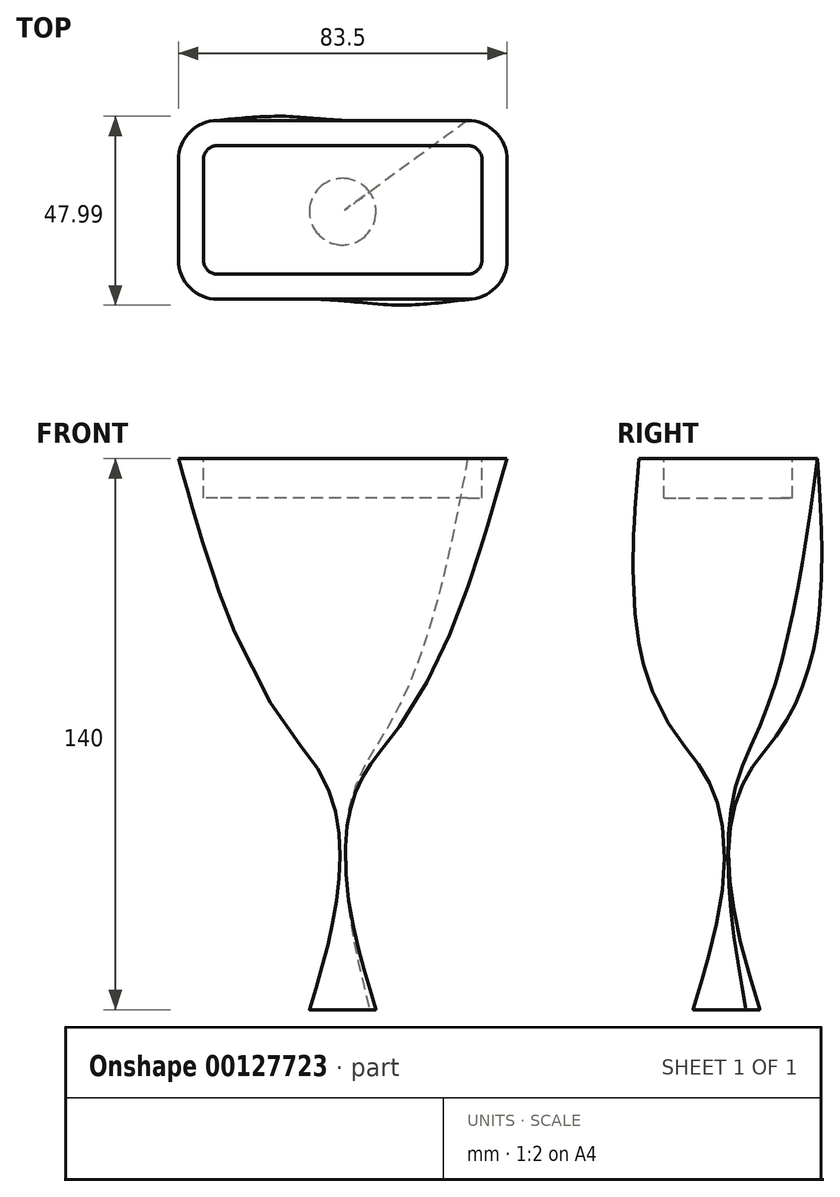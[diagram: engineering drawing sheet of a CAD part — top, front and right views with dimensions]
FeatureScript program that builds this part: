
annotation { "Feature Type Name" : "Feature", "Feature Type Description" : "" }
export const myFeature = defineFeature(function(context is Context, id is Id, definition is map)
    precondition{}
    {
        {
            var Q0;
            Q0=qCreatedBy(makeId("Top.planeOp"),FACE);
            cPlane(context, id + "F0", {"entities" : qUnion([Q0]), "cplaneType" : CPlaneType.OFFSET, "offset" : 60 * mm, "width" : 152.4 * mm, "height" : 152.4 * mm});
        }
        {
            var Q0;
            Q0=qCreatedBy(id+"F0.planeOp",FACE);
            var sketch = newSketch(context, id + "F1", { "sketchPlane" : qUnion([Q0])});
            skLineSegment(sketch, "E0.bottom", {"start": v(31.76, 23.15) * mm, "end": v(-31.74, 23.15) * mm});
            skLineSegment(sketch, "E0.top", {"start": v(31.76, -22.25) * mm, "end": v(-31.74, -22.25) * mm});
            skLineSegment(sketch, "E0.left", {"start": v(41.76, 13.15) * mm, "end": v(41.76, -12.25) * mm});
            skLineSegment(sketch, "E0.right", {"start": v(-41.74, 13.15) * mm, "end": v(-41.74, -12.25) * mm});
            skPoint(sketch, "E0.middle", {"position": v(0.01, 0.45) * mm});
            skPoint(sketch, "E1.visualSharp", {"position": v(-41.74, 23.15) * mm});
            skArc(sketch, "E1.filletArc", {"start": v(-31.74, 23.15) * mm, "mid": v(-38.8, 20.22) * mm, "end": v(-41.74, 13.15) * mm});
            skPoint(sketch, "E2.visualSharp", {"position": v(-41.74, -22.25) * mm});
            skArc(sketch, "E2.filletArc", {"start": v(-41.74, -12.25) * mm, "mid": v(-38.8, -19.32) * mm, "end": v(-31.74, -22.25) * mm});
            skPoint(sketch, "E3.visualSharp", {"position": v(41.76, -22.25) * mm});
            skArc(sketch, "E3.filletArc", {"start": v(31.76, -22.25) * mm, "mid": v(38.84, -19.32) * mm, "end": v(41.76, -12.25) * mm});
            skPoint(sketch, "E4.visualSharp", {"position": v(41.76, 23.15) * mm});
            skArc(sketch, "E4.filletArc", {"start": v(41.76, 13.15) * mm, "mid": v(38.84, 20.22) * mm, "end": v(31.76, 23.15) * mm});
            skSolve(sketch);
        }
        {
            var Q0;
            Q0=qCreatedBy(makeId("Top.planeOp"),FACE);
            cPlane(context, id + "F2", {"entities" : qUnion([Q0]), "cplaneType" : CPlaneType.OFFSET, "offset" : 10 * mm, "oppositeDirection" : true, "width" : 152.4 * mm, "height" : 152.4 * mm});
        }
        {
            var Q0;
            Q0=qCreatedBy(id+"F2.planeOp",FACE);
            var sketch = newSketch(context, id + "F3", { "sketchPlane" : qUnion([Q0])});
            skCircle(sketch, "E5", {"center": v(0, 0) * mm, "radius": 12.93 * mm});
            skSolve(sketch);
        }
        {
            var Q0;
            Q0=qCreatedBy(makeId("Top.planeOp"),FACE);
            cPlane(context, id + "F4", {"entities" : qUnion([Q0]), "cplaneType" : CPlaneType.OFFSET, "offset" : 20 * mm, "oppositeDirection" : true, "width" : 152.4 * mm, "height" : 152.4 * mm});
        }
        {
            var Q0;
            Q0=qCreatedBy(id+"F4.planeOp",FACE);
            var sketch = newSketch(context, id + "F5", { "sketchPlane" : qUnion([Q0])});
            skCircle(sketch, "E6", {"center": v(0, 0) * mm, "radius": 5.59 * mm});
            skSolve(sketch);
        }
        {
            var Q0;
            Q0=qCreatedBy(id+"F4.planeOp",FACE);
            cPlane(context, id + "F6", {"entities" : qUnion([Q0]), "cplaneType" : CPlaneType.OFFSET, "offset" : 50 * mm, "oppositeDirection" : true, "width" : 152.4 * mm, "height" : 152.4 * mm});
        }
        {
            var Q0;
            Q0=qCreatedBy(id+"F6.planeOp",FACE);
            var sketch = newSketch(context, id + "F7", { "sketchPlane" : qUnion([Q0])});
            skCircle(sketch, "E7", {"center": v(0, 0) * mm, "radius": 5.47 * mm});
            skSolve(sketch);
        }
        {
            var Q0;
            Q0=qCreatedBy(id+"F6.planeOp",FACE);
            cPlane(context, id + "F8", {"entities" : qUnion([Q0]), "cplaneType" : CPlaneType.OFFSET, "offset" : 10 * mm, "oppositeDirection" : true, "width" : 152.4 * mm, "height" : 152.4 * mm});
        }
        {
            var Q0;
            Q0=qCreatedBy(id+"F8.planeOp",FACE);
            var sketch = newSketch(context, id + "F9", { "sketchPlane" : qUnion([Q0])});
            skCircle(sketch, "E8", {"center": v(0, 0) * mm, "radius": 8.46 * mm});
            skSolve(sketch);
        }
        {
            var Q0;
            Q0 = qSketchRegion(id + "F1", true);
            var Q1;
            Q1 = qSketchRegion(id + "F3", true);
            var Q2;
            Q2 = qSketchRegion(id + "F5", true);
            var Q3;
            Q3 = qSketchRegion(id + "F7", true);
            var Q4;
            Q4 = qSketchRegion(id + "F9", true);
            loft(context, id + "F10", {"sheetProfilesArray" : [{ "sheetProfileEntities" : qUnion([Q0]) }, { "sheetProfileEntities" : qUnion([Q1]) }, { "sheetProfileEntities" : qUnion([Q2]) }, { "sheetProfileEntities" : qUnion([Q3]) }, { "sheetProfileEntities" : qUnion([Q4]) }]});
        }
        {
            var Q0;
            Q0=makeQuery(id+"F10.opLoft","CAP_FACE",FACE,{"disambiguationData":[OSD([makeQuery(id+"F1.imprint","IMPRINT",FACE,{"disambiguationData":[TD([[makeQuery(id+"F1.imprint","IMPRINT",EDGE,{"derivedFrom":sQuery(id+"F1.wireOp",EDGE,"E0.bottom")}),1.0]])]})])],"isStart":true});
            var sketch = newSketch(context, id + "F11", { "sketchPlane" : qUnion([Q0])});
            skFitSpline(sketch, "E9.0", {"points": [v(35.41, -12.25) * mm, v(35.41, -3.79) * mm, v(35.41, 4.68) * mm, v(35.41, 13.15) * mm]});
            skFitSpline(sketch, "E9.1", {"points": [v(31.76, -15.9) * mm, v(31.89, -15.9) * mm, v(32.06, -15.9) * mm, v(32.3, -15.86) * mm, v(32.48, -15.83) * mm, v(32.65, -15.8) * mm, v(32.82, -15.75) * mm, v(33, -15.7) * mm, v(33.16, -15.63) * mm, v(33.33, -15.55) * mm, v(33.49, -15.47) * mm, v(33.64, -15.39) * mm, v(33.8, -15.29) * mm, v(33.94, -15.18) * mm, v(34.08, -15.08) * mm, v(34.21, -14.96) * mm, v(34.35, -14.83) * mm, v(34.47, -14.7) * mm, v(34.59, -14.57) * mm, v(34.7, -14.43) * mm, v(34.8, -14.28) * mm, v(34.9, -14.13) * mm, v(34.98, -13.97) * mm, v(35.06, -13.82) * mm, v(35.14, -13.65) * mm, v(35.2, -13.48) * mm, v(35.26, -13.31) * mm, v(35.3, -13.14) * mm, v(35.36, -12.9) * mm, v(35.4, -12.61) * mm, v(35.41, -12.37) * mm, v(35.41, -12.25) * mm]});
            skFitSpline(sketch, "E9.2", {"points": [v(35.41, 13.15) * mm, v(35.41, 13.27) * mm, v(35.4, 13.45) * mm, v(35.38, 13.68) * mm, v(35.35, 13.86) * mm, v(35.3, 14.04) * mm, v(35.26, 14.2) * mm, v(35.2, 14.38) * mm, v(35.14, 14.55) * mm, v(35.06, 14.71) * mm, v(34.98, 14.87) * mm, v(34.9, 15.02) * mm, v(34.8, 15.18) * mm, v(34.7, 15.32) * mm, v(34.59, 15.46) * mm, v(34.47, 15.6) * mm, v(34.35, 15.73) * mm, v(34.22, 15.85) * mm, v(34.08, 15.97) * mm, v(33.94, 16.08) * mm, v(33.8, 16.18) * mm, v(33.64, 16.28) * mm, v(33.49, 16.37) * mm, v(33.33, 16.45) * mm, v(33.16, 16.52) * mm, v(33, 16.59) * mm, v(32.82, 16.64) * mm, v(32.65, 16.69) * mm, v(32.42, 16.74) * mm, v(32.12, 16.79) * mm, v(31.89, 16.8) * mm, v(31.76, 16.8) * mm]});
            skFitSpline(sketch, "E9.3", {"points": [v(-31.74, -15.9) * mm, v(-10.57, -15.9) * mm, v(10.6, -15.9) * mm, v(31.76, -15.9) * mm]});
            skFitSpline(sketch, "E9.4", {"points": [v(31.76, 16.8) * mm, v(10.6, 16.8) * mm, v(-10.57, 16.8) * mm, v(-31.74, 16.8) * mm]});
            skFitSpline(sketch, "E9.5", {"points": [v(-31.74, 16.8) * mm, v(-31.86, 16.8) * mm, v(-32.03, 16.79) * mm, v(-32.27, 16.76) * mm, v(-32.45, 16.73) * mm, v(-32.62, 16.69) * mm, v(-32.8, 16.64) * mm, v(-32.96, 16.59) * mm, v(-33.13, 16.52) * mm, v(-33.3, 16.45) * mm, v(-33.46, 16.37) * mm, v(-33.61, 16.28) * mm, v(-33.76, 16.18) * mm, v(-33.91, 16.08) * mm, v(-34.05, 15.97) * mm, v(-34.19, 15.85) * mm, v(-34.32, 15.73) * mm, v(-34.44, 15.6) * mm, v(-34.56, 15.46) * mm, v(-34.67, 15.32) * mm, v(-34.77, 15.18) * mm, v(-34.87, 15.02) * mm, v(-34.96, 14.87) * mm, v(-35.04, 14.71) * mm, v(-35.1, 14.54) * mm, v(-35.17, 14.38) * mm, v(-35.23, 14.2) * mm, v(-35.28, 14.04) * mm, v(-35.33, 13.8) * mm, v(-35.37, 13.5) * mm, v(-35.39, 13.27) * mm, v(-35.39, 13.15) * mm]});
            skFitSpline(sketch, "E9.6", {"points": [v(-35.39, 13.15) * mm, v(-35.39, 4.68) * mm, v(-35.39, -3.79) * mm, v(-35.39, -12.25) * mm]});
            skFitSpline(sketch, "E9.7", {"points": [v(-35.39, -12.25) * mm, v(-35.39, -12.37) * mm, v(-35.38, -12.55) * mm, v(-35.35, -12.79) * mm, v(-35.32, -12.97) * mm, v(-35.28, -13.14) * mm, v(-35.23, -13.31) * mm, v(-35.17, -13.48) * mm, v(-35.1, -13.65) * mm, v(-35.04, -13.82) * mm, v(-34.96, -13.97) * mm, v(-34.87, -14.13) * mm, v(-34.77, -14.28) * mm, v(-34.67, -14.43) * mm, v(-34.56, -14.57) * mm, v(-34.44, -14.7) * mm, v(-34.32, -14.84) * mm, v(-34.19, -14.96) * mm, v(-34.05, -15.08) * mm, v(-33.91, -15.18) * mm, v(-33.76, -15.29) * mm, v(-33.61, -15.39) * mm, v(-33.46, -15.47) * mm, v(-33.3, -15.55) * mm, v(-33.13, -15.63) * mm, v(-32.96, -15.7) * mm, v(-32.8, -15.75) * mm, v(-32.63, -15.8) * mm, v(-32.39, -15.85) * mm, v(-32.1, -15.9) * mm, v(-31.86, -15.9) * mm, v(-31.74, -15.9) * mm]});
            skSolve(sketch);
        }
        {
            var Q0;
            Q0 = qSketchRegion(id + "F11", true);
            extrude(context, id + "F12", {"entities" : qUnion([Q0]), "operationType" : NewBodyOperationType.REMOVE, "oppositeDirection" : true, "depth" : 10 * mm});
        }
    });
